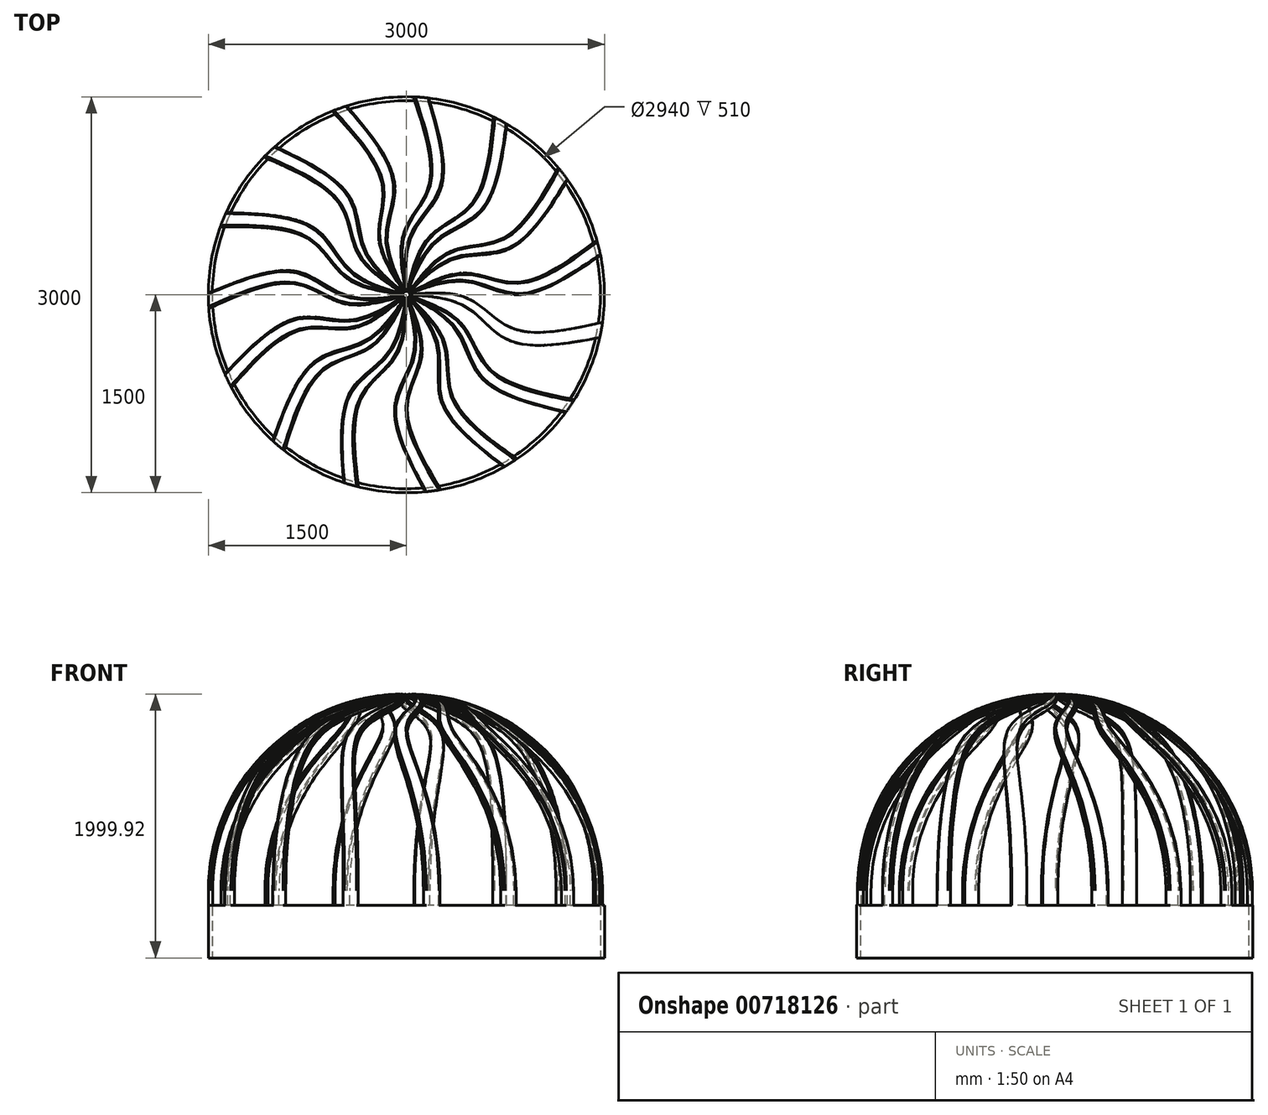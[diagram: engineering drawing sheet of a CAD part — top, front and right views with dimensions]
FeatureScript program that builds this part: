
annotation { "Feature Type Name" : "Feature", "Feature Type Description" : "" }
export const myFeature = defineFeature(function(context is Context, id is Id, definition is map)
    precondition{}
    {
        {
            var Q0;
            Q0=qCreatedBy(makeId("Top.planeOp"),FACE);
            var sketch = newSketch(context, id + "F0", { "sketchPlane" : qUnion([Q0])});
            skCircle(sketch, "E0", {"center": v(0, 0) * mm, "radius": 1500 * mm});
            skSolve(sketch);
        }
        {
            var Q0;
            Q0=makeQuery(id+"F0.imprint","IMPRINT",FACE,{"disambiguationData":[TD([[makeQuery(id+"F0.imprint","IMPRINT",EDGE,{"derivedFrom":sQuery(id+"F0.wireOp",EDGE,"E0")}),1.0]])]});
            extrude(context, id + "F1", {"entities" : qUnion([Q0]), "depth" : 2000 * mm, "offsetDistance" : 25 * mm});
        }
        {
            var Q0;
            Q0=makeQuery(id+"F1.opExtrude","CAP_FACE",FACE,{"disambiguationData":[OSD([sQuery(id+"F0.wireOp",EDGE,"E0")])],"isStart":false});
            fillet(context, id + "F2", {"entities" : qUnion([Q0]), "radius" : 1490 * mm, "tangentPropagation" : true, "allowEdgeOverflow" : false});
        }
        {
            var Q0;
            Q0=makeQuery(id+"F1.opExtrude","CAP_FACE",FACE,{"disambiguationData":[OSD([sQuery(id+"F0.wireOp",EDGE,"E0")])],"isStart":true});
            shell(context, id + "F3", {"entities" : qUnion([Q0]), "thickness" : 30 * mm});
        }
        {
            var Q0;
            Q0=makeQuery(id+"F1.opExtrude","CAP_FACE",FACE,{"disambiguationData":[OSD([sQuery(id+"F0.wireOp",EDGE,"E0")])],"isStart":false});
            var sketch = newSketch(context, id + "F4", { "sketchPlane" : qUnion([Q0])});
            skLineSegment(sketch, "E1", {"start": v(0, 0) * mm, "end": v(0, 0) * mm});
            skFitSpline(sketch, "E2", {"points": [v(0, 0) * mm, v(443.42, 164.47) * mm, v(843.7, 94.34) * mm, v(1455.44, 423.4) * mm], "startDerivative": vector(1720.93, 881.17) * mm, "endDerivative": vector(1641.37, 1335.09) * mm, "construction": true});
            skPoint(sketch, "E3.2.0", {"position": v(338.19, 330.6) * mm});
            skPoint(sketch, "E3.2.1", {"position": v(374.7, 275.35) * mm});
            skPoint(sketch, "E3.2.2", {"position": v(778.83, 346.76) * mm});
            skPoint(sketch, "E3.2.3", {"position": v(732.39, 429.34) * mm});
            skPoint(sketch, "E3.2.4", {"position": v(1157.4, 978.78) * mm});
            skPoint(sketch, "E3.2.5", {"position": v(1235.82, 895.92) * mm});
            skPoint(sketch, "E3.4.0", {"position": v(174.48, 439.57) * mm});
            skPoint(sketch, "E3.4.1", {"position": v(230.3, 403.95) * mm});
            skPoint(sketch, "E3.4.2", {"position": v(570.46, 633.56) * mm});
            skPoint(sketch, "E3.4.3", {"position": v(494.44, 690.11) * mm});
            skPoint(sketch, "E3.4.4", {"position": v(659.23, 1364.92) * mm});
            skPoint(sketch, "E3.4.5", {"position": v(764.57, 1321.12) * mm});
            skPoint(sketch, "E3.6.0", {"position": v(-19.4, 472.54) * mm});
            skPoint(sketch, "E3.6.1", {"position": v(46.1, 462.7) * mm});
            skPoint(sketch, "E3.6.2", {"position": v(263.45, 810.8) * mm});
            skPoint(sketch, "E3.6.3", {"position": v(171, 831.56) * mm});
            skPoint(sketch, "E3.6.4", {"position": v(47.07, 1515.05) * mm});
            skPoint(sketch, "E3.6.5", {"position": v(161.12, 1517.88) * mm});
            skPoint(sketch, "E3.8.0", {"position": v(-209.91, 423.8) * mm});
            skPoint(sketch, "E3.8.1", {"position": v(-146.09, 441.44) * mm});
            skPoint(sketch, "E3.8.2", {"position": v(-89.11, 847.86) * mm});
            skPoint(sketch, "E3.8.3", {"position": v(-182, 829.21) * mm});
            skPoint(sketch, "E3.8.4", {"position": v(-573.22, 1403.21) * mm});
            skPoint(sketch, "E3.8.5", {"position": v(-470.18, 1452.19) * mm});
            skPoint(sketch, "E3.10.0", {"position": v(-364.14, 301.78) * mm});
            skPoint(sketch, "E3.10.1", {"position": v(-313, 343.86) * mm});
            skPoint(sketch, "E3.10.2", {"position": v(-426.27, 738.32) * mm});
            skPoint(sketch, "E3.10.3", {"position": v(-503.55, 683.5) * mm});
            skPoint(sketch, "E3.10.4", {"position": v(-1094.4, 1048.75) * mm});
            skPoint(sketch, "E3.10.5", {"position": v(-1020.19, 1135.4) * mm});
            skPoint(sketch, "E3.12.0", {"position": v(-455.4, 127.58) * mm});
            skPoint(sketch, "E3.12.1", {"position": v(-425.8, 186.82) * mm});
            skPoint(sketch, "E3.12.2", {"position": v(-689.71, 501.1) * mm});
            skPoint(sketch, "E3.12.3", {"position": v(-738.01, 419.6) * mm});
            skPoint(sketch, "E3.12.4", {"position": v(-1426.35, 512.95) * mm});
            skPoint(sketch, "E3.12.5", {"position": v(-1393.8, 622.29) * mm});
            skPoint(sketch, "E3.14.0", {"position": v(-467.92, -68.68) * mm});
            skPoint(sketch, "E3.14.1", {"position": v(-464.98, -2.53) * mm});
            skPoint(sketch, "E3.14.2", {"position": v(-833.9, 177.25) * mm});
            skPoint(sketch, "E3.14.3", {"position": v(-844.87, 83.14) * mm});
            skPoint(sketch, "E3.14.4", {"position": v(-1511.67, -111.55) * mm});
            skPoint(sketch, "E3.14.5", {"position": v(-1526.4, 1.58) * mm});
            skPoint(sketch, "E3.16.0", {"position": v(-399.53, -253.06) * mm});
            skPoint(sketch, "E3.16.1", {"position": v(-423.75, -191.43) * mm});
            skPoint(sketch, "E3.16.2", {"position": v(-833.9, -177.25) * mm});
            skPoint(sketch, "E3.16.3", {"position": v(-805.65, -267.69) * mm});
            skPoint(sketch, "E3.16.4", {"position": v(-1335.6, -716.76) * mm});
            skPoint(sketch, "E3.16.5", {"position": v(-1395.08, -619.4) * mm});
            skPoint(sketch, "E3.18.0", {"position": v(-262.06, -393.7) * mm});
            skPoint(sketch, "E3.18.1", {"position": v(-309.26, -347.24) * mm});
            skPoint(sketch, "E3.18.2", {"position": v(-689.71, -501.1) * mm});
            skPoint(sketch, "E3.18.3", {"position": v(-627.12, -572.23) * mm});
            skPoint(sketch, "E3.18.4", {"position": v(-928.6, -1198.03) * mm});
            skPoint(sketch, "E3.18.5", {"position": v(-1022.54, -1133.28) * mm});
            skPoint(sketch, "E3.20.0", {"position": v(-79.28, -466.24) * mm});
            skPoint(sketch, "E3.20.1", {"position": v(-141.28, -443) * mm});
            skPoint(sketch, "E3.20.2", {"position": v(-426.27, -738.32) * mm});
            skPoint(sketch, "E3.20.3", {"position": v(-340.15, -777.83) * mm});
            skPoint(sketch, "E3.20.4", {"position": v(-361.04, -1472.15) * mm});
            skPoint(sketch, "E3.20.5", {"position": v(-473.19, -1451.2) * mm});
            skPoint(sketch, "E3.22.0", {"position": v(117.22, -458.18) * mm});
            skPoint(sketch, "E3.22.1", {"position": v(51.12, -462.17) * mm});
            skPoint(sketch, "E3.22.2", {"position": v(-89.11, -847.86) * mm});
            skPoint(sketch, "E3.22.3", {"position": v(5.63, -848.94) * mm});
            skPoint(sketch, "E3.22.4", {"position": v(268.95, -1491.73) * mm});
            skPoint(sketch, "E3.22.5", {"position": v(157.98, -1518.2) * mm});
            skPoint(sketch, "E3.24.0", {"position": v(293.44, -370.9) * mm});
            skPoint(sketch, "E3.24.1", {"position": v(234.68, -401.42) * mm});
            skPoint(sketch, "E3.24.2", {"position": v(263.45, -810.8) * mm});
            skPoint(sketch, "E3.24.3", {"position": v(350.44, -773.25) * mm});
            skPoint(sketch, "E3.24.4", {"position": v(852.44, -1253.37) * mm});
            skPoint(sketch, "E3.24.5", {"position": v(761.83, -1322.7) * mm});
            skPoint(sketch, "E3.26.0", {"position": v(418.93, -219.48) * mm});
            skPoint(sketch, "E3.26.1", {"position": v(377.66, -271.27) * mm});
            skPoint(sketch, "E3.26.2", {"position": v(570.46, -633.56) * mm});
            skPoint(sketch, "E3.26.3", {"position": v(634.65, -563.87) * mm});
            skPoint(sketch, "E3.26.4", {"position": v(1288.53, -798.3) * mm});
            skPoint(sketch, "E3.26.5", {"position": v(1233.96, -898.48) * mm});
            skPoint(sketch, "E3.27.3", {"position": v(738.01, -419.6) * mm});
            skPoint(sketch, "E3.28.0", {"position": v(471.98, -30.1) * mm});
            skPoint(sketch, "E3.28.1", {"position": v(455.34, -94.2) * mm});
            skPoint(sketch, "E3.28.2", {"position": v(778.83, -346.76) * mm});
            skPoint(sketch, "E3.28.3", {"position": v(809.13, -256.98) * mm});
            skPoint(sketch, "E3.28.4", {"position": v(1501.83, -205.18) * mm});
            skPoint(sketch, "E3.28.5", {"position": v(1492.72, -318.9) * mm});
            skFitSpline(sketch, "E4", {"points": [v(0, 0) * mm, v(374.7, 275.35) * mm, v(778.83, 346.76) * mm, v(1235.82, 895.92) * mm], "startDerivative": vector(1131.7, 1116.14) * mm, "endDerivative": vector(1100.53, 1804.63) * mm});
            skFitSpline(sketch, "E5", {"points": [v(0, 0) * mm, v(338.19, 330.6) * mm, v(732.39, 429.34) * mm, v(1157.4, 978.78) * mm], "startDerivative": vector(974.1, 1303.77) * mm, "endDerivative": vector(1012.18, 1800.98) * mm});
            skFitSpline(sketch, "E6", {"points": [v(0, 0) * mm, v(230.3, 403.95) * mm, v(570.46, 633.56) * mm, v(764.57, 1321.12) * mm], "startDerivative": vector(579.9, 1479.95) * mm, "endDerivative": vector(271.37, 2096.24) * mm});
            skFitSpline(sketch, "E7", {"points": [v(0, 0) * mm, v(174.48, 439.57) * mm, v(494.44, 690.11) * mm, v(659.23, 1364.92) * mm], "startDerivative": vector(359.6, 1587.25) * mm, "endDerivative": vector(192.15, 2056.97) * mm});
            skFitSpline(sketch, "E8", {"points": [v(0, 0) * mm, v(46.1, 462.7) * mm, v(263.45, 810.8) * mm, v(161.12, 1517.88) * mm], "startDerivative": vector(-72.2, 1587.87) * mm, "endDerivative": vector(-604.7, 2025.39) * mm});
            skFitSpline(sketch, "E9", {"points": [v(0, 0) * mm, v(-19.4, 472.54) * mm, v(171, 831.56) * mm, v(47.07, 1515.05) * mm], "startDerivative": vector(-317.1, 1596.29) * mm, "endDerivative": vector(-661.1, 1957.29) * mm});
            skFitSpline(sketch, "E10", {"points": [v(0, 0) * mm, v(-146.09, 441.44) * mm, v(-89.11, 847.86) * mm, v(-470.18, 1452.19) * mm], "startDerivative": vector(-711.8, 1421.22) * mm, "endDerivative": vector(-1376.22, 1604.33) * mm});
            skFitSpline(sketch, "E11", {"points": [v(0, 0) * mm, v(-209.91, 423.8) * mm, v(-182, 829.21) * mm, v(-573.22, 1403.21) * mm], "startDerivative": vector(-938.95, 1329.3) * mm, "endDerivative": vector(-1400.05, 1519.18) * mm});
            skFitSpline(sketch, "E12", {"points": [v(0, 0) * mm, v(-313, 343.86) * mm, v(-426.27, 738.32) * mm, v(-1020.19, 1135.4) * mm], "startDerivative": vector(-1228.32, 1008.84) * mm, "endDerivative": vector(-1909.78, 905.86) * mm});
            skFitSpline(sketch, "E13", {"points": [v(0, 0) * mm, v(-364.14, 301.78) * mm, v(-503.55, 683.5) * mm, v(-1094.4, 1048.75) * mm], "startDerivative": vector(-1398.45, 832.48) * mm, "endDerivative": vector(-1896.92, 818.38) * mm});
            skFitSpline(sketch, "E14", {"points": [v(0, 0) * mm, v(-425.8, 186.82) * mm, v(-689.71, 501.1) * mm, v(-1393.8, 622.29) * mm], "startDerivative": vector(-1532.46, 422.02) * mm, "endDerivative": vector(-2113.12, 50.77) * mm});
            skFitSpline(sketch, "E15", {"points": [v(0, 0) * mm, v(-455.4, 127.58) * mm, v(-738.01, 419.6) * mm, v(-1426.35, 512.95) * mm], "startDerivative": vector(-1616.15, 191.7) * mm, "endDerivative": vector(-2065.79, -23.92) * mm});
            skFitSpline(sketch, "E16", {"points": [v(0, 0) * mm, v(-464.98, -2.53) * mm, v(-833.9, 177.25) * mm, v(-1526.4, 1.58) * mm], "startDerivative": vector(-1571.62, -237.77) * mm, "endDerivative": vector(-1951.08, -813.1) * mm});
            skFitSpline(sketch, "E17", {"points": [v(0, 0) * mm, v(-467.92, -68.68) * mm, v(-844.87, 83.14) * mm, v(-1511.67, -111.55) * mm], "startDerivative": vector(-1554.4, -482.21) * mm, "endDerivative": vector(-1877.46, -862.08) * mm});
            skFitSpline(sketch, "E18", {"points": [v(0, 0) * mm, v(-423.75, -191.43) * mm, v(-833.9, -177.25) * mm, v(-1395.08, -619.4) * mm], "startDerivative": vector(-1339.04, -856.45) * mm, "endDerivative": vector(-1451.68, -1536.38) * mm});
            skFitSpline(sketch, "E19", {"points": [v(0, 0) * mm, v(-399.53, -253.06) * mm, v(-805.65, -267.69) * mm, v(-1335.6, -716.76) * mm], "startDerivative": vector(-1223.88, -1072.75) * mm, "endDerivative": vector(-1364.5, -1551.18) * mm});
            skFitSpline(sketch, "E20", {"points": [v(0, 0) * mm, v(-309.26, -347.24) * mm, v(-689.71, -501.1) * mm, v(-1022.54, -1133.28) * mm], "startDerivative": vector(-874.92, -1327.04) * mm, "endDerivative": vector(-701.28, -1994) * mm});
            skFitSpline(sketch, "E21", {"points": [v(0, 0) * mm, v(-262.06, -393.7) * mm, v(-627.12, -572.23) * mm, v(-928.6, -1198.03) * mm], "startDerivative": vector(-681.74, -1477.8) * mm, "endDerivative": vector(-615.62, -1972.07) * mm});
            skFitSpline(sketch, "E22", {"points": [v(0, 0) * mm, v(-141.28, -443) * mm, v(-426.27, -738.32) * mm, v(-473.19, -1451.2) * mm], "startDerivative": vector(-259.52, -1568.18) * mm, "endDerivative": vector(170.39, -2106.85) * mm});
            skFitSpline(sketch, "E23", {"points": [v(0, 0) * mm, v(-79.28, -466.24) * mm, v(-340.15, -777.83) * mm, v(-361.04, -1472.15) * mm], "startDerivative": vector(-21.73, -1627.33) * mm, "endDerivative": vector(239.72, -2051.97) * mm});
            skFitSpline(sketch, "E24", {"points": [v(0, 0) * mm, v(51.12, -462.17) * mm, v(-89.11, -847.86) * mm, v(157.98, -1518.2) * mm], "startDerivative": vector(400.75, -1538.16) * mm, "endDerivative": vector(1012.6, -1855.4) * mm});
            skFitSpline(sketch, "E25", {"points": [v(0, 0) * mm, v(117.22, -458.18) * mm, v(5.63, -848.94) * mm, v(268.95, -1491.73) * mm], "startDerivative": vector(642.05, -1495.48) * mm, "endDerivative": vector(1053.6, -1777.07) * mm});
            skFitSpline(sketch, "E26", {"points": [v(0, 0) * mm, v(234.68, -401.42) * mm, v(263.45, -810.8) * mm, v(761.83, -1322.7) * mm], "startDerivative": vector(991.73, -1242.18) * mm, "endDerivative": vector(1679.7, -1283.13) * mm});
            skFitSpline(sketch, "E27", {"points": [v(0, 0) * mm, v(293.44, -370.9) * mm, v(350.44, -773.25) * mm, v(852.44, -1253.37) * mm], "startDerivative": vector(1194.8, -1105.04) * mm, "endDerivative": vector(1685.31, -1194.9) * mm});
            skFitSpline(sketch, "E28", {"points": [v(0, 0) * mm, v(377.66, -271.27) * mm, v(570.46, -633.56) * mm, v(1233.96, -898.48) * mm], "startDerivative": vector(1411.23, -731.41) * mm, "endDerivative": vector(2056.39, -489) * mm});
            skFitSpline(sketch, "E29", {"points": [v(0, 0) * mm, v(418.93, -219.48) * mm, v(634.65, -563.87) * mm, v(1288.53, -798.3) * mm], "startDerivative": vector(1540.97, -523.54) * mm, "endDerivative": vector(2025.62, -406.1) * mm});
            skFitSpline(sketch, "E30", {"points": [v(0, 0) * mm, v(455.34, -94.2) * mm, v(778.83, -346.76) * mm, v(1492.72, -318.9) * mm], "startDerivative": vector(1586.71, -94.18) * mm, "endDerivative": vector(2077.5, 389.68) * mm});
            skFitSpline(sketch, "E31", {"points": [v(-4.96, -0.45) * mm, v(471.98, -30.1) * mm, v(809.13, -256.98) * mm, v(1501.83, -205.18) * mm], "startDerivative": vector(1626.2, 146.66) * mm, "endDerivative": vector(2017.33, 453.02) * mm});
            skFitSpline(sketch, "E32", {"points": [v(0, 0) * mm, v(454.3, 99.15) * mm, v(852.53, 0) * mm, v(1493.38, 315.81) * mm], "startDerivative": vector(1487.84, 559.34) * mm, "endDerivative": vector(1739.4, 1200.99) * mm});
            skFitSpline(sketch, "E33", {"points": [v(0, 0) * mm, v(443.42, 164.47) * mm, v(843.7, 94.34) * mm, v(1455.44, 423.4) * mm], "startDerivative": vector(1420.17, 794.85) * mm, "endDerivative": vector(1657.2, 1233.59) * mm});
            skFitSpline(sketch, "E34.trimOffspring", {"points": [v(0, 0) * mm, v(454.3, 99.15) * mm, v(852.53, 0) * mm, v(1493.38, 315.81) * mm], "startDerivative": vector(1487.84, 559.34) * mm, "endDerivative": vector(1620.1, 1322.46) * mm, "construction": true});
            skArc(sketch, "E35", {"start": v(-19.31, 15.87) * mm, "mid": v(-20.45, 14.38) * mm, "end": v(-21.47, 12.8) * mm});
            skArc(sketch, "E36.trimOffspring", {"start": v(-11.19, 22.36) * mm, "mid": v(-12.84, 21.45) * mm, "end": v(-14.41, 20.43) * mm});
            skArc(sketch, "E37.trimOffspring", {"start": v(-1.13, 24.97) * mm, "mid": v(-3, 24.82) * mm, "end": v(-4.86, 24.52) * mm});
            skArc(sketch, "E38.trimOffspring", {"start": v(9.13, 23.27) * mm, "mid": v(7.35, 23.9) * mm, "end": v(5.54, 24.38) * mm});
            skArc(sketch, "E39.trimOffspring", {"start": v(17.8, 17.55) * mm, "mid": v(16.44, 18.84) * mm, "end": v(14.97, 20.02) * mm});
            skArc(sketch, "E40.trimOffspring", {"start": v(23.4, 8.78) * mm, "mid": v(22.68, 10.52) * mm, "end": v(21.82, 12.2) * mm});
            skArc(sketch, "E41.trimOffspring", {"start": v(24.96, -1.49) * mm, "mid": v(25, 0.37) * mm, "end": v(24.9, 2.23) * mm});
            skArc(sketch, "E42.trimOffspring", {"start": v(22.2, -11.51) * mm, "mid": v(23, -9.81) * mm, "end": v(23.67, -8.05) * mm});
            skArc(sketch, "E43.trimOffspring", {"start": v(15.6, -19.54) * mm, "mid": v(17.02, -18.32) * mm, "end": v(18.34, -16.98) * mm});
            skArc(sketch, "E44.trimOffspring", {"start": v(6.3, -24.2) * mm, "mid": v(8.1, -23.65) * mm, "end": v(9.85, -22.98) * mm});
            skArc(sketch, "E45.trimOffspring", {"start": v(-4.1, -24.66) * mm, "mid": v(-2.22, -24.9) * mm, "end": v(-0.35, -25) * mm});
            skArc(sketch, "E46.trimOffspring", {"start": v(-13.77, -20.87) * mm, "mid": v(-12.16, -21.84) * mm, "end": v(-10.48, -22.7) * mm});
            skArc(sketch, "E47.trimOffspring", {"start": v(-21.07, -13.46) * mm, "mid": v(-20, -15) * mm, "end": v(-18.8, -16.47) * mm});
            skArc(sketch, "E48.trimOffspring", {"start": v(-24.72, -3.73) * mm, "mid": v(-24.37, -5.58) * mm, "end": v(-23.88, -7.4) * mm});
            skArc(sketch, "E49.trimOffspring", {"start": v(-24.1, 6.65) * mm, "mid": v(-24.53, 4.82) * mm, "end": v(-24.82, 2.96) * mm});
            skLineSegment(sketch, "E50", {"start": v(-1511.67, -111.55) * mm, "end": v(-1560.88, -374.04) * mm});
            skLineSegment(sketch, "E51", {"start": v(-1560.88, -374.04) * mm, "end": v(-1395.08, -619.4) * mm});
            skLineSegment(sketch, "E52", {"start": v(-1335.6, -716.76) * mm, "end": v(-1218.07, -1088.2) * mm});
            skLineSegment(sketch, "E53", {"start": v(-1218.07, -1088.2) * mm, "end": v(-1022.54, -1133.28) * mm});
            skLineSegment(sketch, "E54", {"start": v(-1526.4, 1.58) * mm, "end": v(-1643.98, 215.48) * mm});
            skLineSegment(sketch, "E55", {"start": v(-1643.98, 215.48) * mm, "end": v(-1426.35, 512.95) * mm});
            skLineSegment(sketch, "E56", {"start": v(-1393.8, 622.29) * mm, "end": v(-1393.8, 869.3) * mm});
            skLineSegment(sketch, "E57", {"start": v(-1393.8, 869.3) * mm, "end": v(-1094.4, 1048.75) * mm});
            skLineSegment(sketch, "E58", {"start": v(-1020.19, 1135.4) * mm, "end": v(-928.65, 1338.53) * mm});
            skLineSegment(sketch, "E59", {"start": v(-928.65, 1338.53) * mm, "end": v(-573.22, 1403.21) * mm});
            skLineSegment(sketch, "E60", {"start": v(-470.18, 1452.19) * mm, "end": v(-366.73, 1522.16) * mm});
            skLineSegment(sketch, "E61", {"start": v(-366.73, 1522.16) * mm, "end": v(47.07, 1515.05) * mm});
            skLineSegment(sketch, "E62", {"start": v(161.12, 1517.88) * mm, "end": v(408.21, 1517.88) * mm});
            skLineSegment(sketch, "E63", {"start": v(408.21, 1517.88) * mm, "end": v(659.23, 1364.92) * mm});
            skLineSegment(sketch, "E64", {"start": v(764.57, 1321.12) * mm, "end": v(962.79, 1239.37) * mm});
            skLineSegment(sketch, "E65", {"start": v(962.79, 1239.37) * mm, "end": v(1157.4, 978.78) * mm});
            skLineSegment(sketch, "E66", {"start": v(1235.82, 895.92) * mm, "end": v(1487.98, 622.29) * mm});
            skLineSegment(sketch, "E67", {"start": v(1487.98, 622.29) * mm, "end": v(1455.44, 423.4) * mm});
            skLineSegment(sketch, "E68", {"start": v(1493.38, 315.81) * mm, "end": v(1598.16, -111.55) * mm});
            skLineSegment(sketch, "E69", {"start": v(1598.16, -111.55) * mm, "end": v(1501.83, -205.18) * mm});
            skLineSegment(sketch, "E70", {"start": v(1492.72, -318.9) * mm, "end": v(1492.72, -519.85) * mm});
            skLineSegment(sketch, "E71", {"start": v(1492.72, -519.85) * mm, "end": v(1288.53, -798.3) * mm});
            skLineSegment(sketch, "E72", {"start": v(1233.96, -898.48) * mm, "end": v(1157.4, -1081.77) * mm});
            skLineSegment(sketch, "E73", {"start": v(1157.4, -1081.77) * mm, "end": v(852.44, -1253.37) * mm});
            skLineSegment(sketch, "E74", {"start": v(761.83, -1322.7) * mm, "end": v(628.57, -1460.06) * mm});
            skLineSegment(sketch, "E75", {"start": v(628.57, -1460.06) * mm, "end": v(268.95, -1491.73) * mm});
            skLineSegment(sketch, "E76", {"start": v(157.98, -1518.2) * mm, "end": v(-58.22, -1548.2) * mm});
            skLineSegment(sketch, "E77", {"start": v(-58.22, -1548.2) * mm, "end": v(-361.04, -1472.15) * mm});
            skLineSegment(sketch, "E78", {"start": v(-473.19, -1451.2) * mm, "end": v(-895.6, -1390.28) * mm});
            skLineSegment(sketch, "E79", {"start": v(-895.6, -1390.28) * mm, "end": v(-928.6, -1198.03) * mm});
            skSolve(sketch);
        }
        {
            var Q0;
            Q0 = qSketchRegion(id + "F4", true);
            extrude(context, id + "F5", {"entities" : qUnion([Q0]), "operationType" : NewBodyOperationType.REMOVE, "oppositeDirection" : true, "depth" : 1600 * mm, "offsetDistance" : 25 * mm});
        }
        {
            var Q0;
            {var subQ0=sQuery(id+"F0.wireOp",EDGE,"E0");Q0=makeQuery(id+"F5.boolean.opBoolean","SPLIT",FACE,{"disambiguationData":[TD([makeQuery(id+"F5.opExtrude","SWEPT_FACE",FACE,{"disambiguationData":[OSD([sQuery(id+"F4.wireOp",EDGE,"E25")])]})])],"derivedFrom":makeQuery(id+"F2.opFillet","BLEND_FACE",FACE,{"disambiguationData":[OSD([subQ0])]})});}
            var Q1;
            {var subQ0=sQuery(id+"F0.wireOp",EDGE,"E0");Q1=makeQuery(id+"F5.boolean.opBoolean","SPLIT",FACE,{"disambiguationData":[TD([makeQuery(id+"F5.opExtrude","SWEPT_FACE",FACE,{"disambiguationData":[OSD([sQuery(id+"F4.wireOp",EDGE,"E27")])]})])],"derivedFrom":makeQuery(id+"F2.opFillet","BLEND_FACE",FACE,{"disambiguationData":[OSD([subQ0])]})});}
            var Q2;
            {var subQ0=sQuery(id+"F0.wireOp",EDGE,"E0");Q2=makeQuery(id+"F5.boolean.opBoolean","SPLIT",FACE,{"disambiguationData":[TD([makeQuery(id+"F5.opExtrude","SWEPT_FACE",FACE,{"disambiguationData":[OSD([sQuery(id+"F4.wireOp",EDGE,"E29")])]})])],"derivedFrom":makeQuery(id+"F2.opFillet","BLEND_FACE",FACE,{"disambiguationData":[OSD([subQ0])]})});}
            var Q3;
            {var subQ0=sQuery(id+"F0.wireOp",EDGE,"E0");Q3=makeQuery(id+"F5.boolean.opBoolean","SPLIT",FACE,{"disambiguationData":[TD([makeQuery(id+"F5.opExtrude","SWEPT_FACE",FACE,{"disambiguationData":[OSD([sQuery(id+"F4.wireOp",EDGE,"E32")])]})])],"derivedFrom":makeQuery(id+"F2.opFillet","BLEND_FACE",FACE,{"disambiguationData":[OSD([subQ0])]})});}
            var Q4;
            {var subQ0=sQuery(id+"F0.wireOp",EDGE,"E0");Q4=makeQuery(id+"F5.boolean.opBoolean","SPLIT",FACE,{"disambiguationData":[TD([makeQuery(id+"F5.opExtrude","SWEPT_FACE",FACE,{"disambiguationData":[OSD([sQuery(id+"F4.wireOp",EDGE,"E4")])]})])],"derivedFrom":makeQuery(id+"F2.opFillet","BLEND_FACE",FACE,{"disambiguationData":[OSD([subQ0])]})});}
            var Q5;
            {var subQ0=sQuery(id+"F0.wireOp",EDGE,"E0");Q5=makeQuery(id+"F5.boolean.opBoolean","SPLIT",FACE,{"disambiguationData":[TD([makeQuery(id+"F5.opExtrude","SWEPT_FACE",FACE,{"disambiguationData":[OSD([sQuery(id+"F4.wireOp",EDGE,"E5")])]})])],"derivedFrom":makeQuery(id+"F2.opFillet","BLEND_FACE",FACE,{"disambiguationData":[OSD([subQ0])]})});}
            var Q6;
            {var subQ0=sQuery(id+"F0.wireOp",EDGE,"E0");Q6=makeQuery(id+"F5.boolean.opBoolean","SPLIT",FACE,{"disambiguationData":[TD([makeQuery(id+"F5.opExtrude","SWEPT_FACE",FACE,{"disambiguationData":[OSD([sQuery(id+"F4.wireOp",EDGE,"E7")])]})])],"derivedFrom":makeQuery(id+"F2.opFillet","BLEND_FACE",FACE,{"disambiguationData":[OSD([subQ0])]})});}
            var Q7;
            {var subQ0=sQuery(id+"F0.wireOp",EDGE,"E0");Q7=makeQuery(id+"F5.boolean.opBoolean","SPLIT",FACE,{"disambiguationData":[TD([makeQuery(id+"F5.opExtrude","SWEPT_FACE",FACE,{"disambiguationData":[OSD([sQuery(id+"F4.wireOp",EDGE,"E9")])]})])],"derivedFrom":makeQuery(id+"F2.opFillet","BLEND_FACE",FACE,{"disambiguationData":[OSD([subQ0])]})});}
            var Q8;
            {var subQ0=sQuery(id+"F0.wireOp",EDGE,"E0");Q8=makeQuery(id+"F5.boolean.opBoolean","SPLIT",FACE,{"disambiguationData":[TD([makeQuery(id+"F5.opExtrude","SWEPT_FACE",FACE,{"disambiguationData":[OSD([sQuery(id+"F4.wireOp",EDGE,"E11")])]})])],"derivedFrom":makeQuery(id+"F2.opFillet","BLEND_FACE",FACE,{"disambiguationData":[OSD([subQ0])]})});}
            var Q9;
            {var subQ0=sQuery(id+"F0.wireOp",EDGE,"E0");Q9=makeQuery(id+"F5.boolean.opBoolean","SPLIT",FACE,{"disambiguationData":[TD([makeQuery(id+"F5.opExtrude","SWEPT_FACE",FACE,{"disambiguationData":[OSD([sQuery(id+"F4.wireOp",EDGE,"E13")])]})])],"derivedFrom":makeQuery(id+"F2.opFillet","BLEND_FACE",FACE,{"disambiguationData":[OSD([subQ0])]})});}
            var Q10;
            {var subQ0=sQuery(id+"F0.wireOp",EDGE,"E0");Q10=makeQuery(id+"F5.boolean.opBoolean","SPLIT",FACE,{"disambiguationData":[TD([makeQuery(id+"F5.opExtrude","SWEPT_FACE",FACE,{"disambiguationData":[OSD([sQuery(id+"F4.wireOp",EDGE,"E15")])]})])],"derivedFrom":makeQuery(id+"F2.opFillet","BLEND_FACE",FACE,{"disambiguationData":[OSD([subQ0])]})});}
            var Q11;
            {var subQ0=sQuery(id+"F0.wireOp",EDGE,"E0");Q11=makeQuery(id+"F5.boolean.opBoolean","SPLIT",FACE,{"disambiguationData":[TD([makeQuery(id+"F5.opExtrude","SWEPT_FACE",FACE,{"disambiguationData":[OSD([sQuery(id+"F4.wireOp",EDGE,"E17")])]})])],"derivedFrom":makeQuery(id+"F2.opFillet","BLEND_FACE",FACE,{"disambiguationData":[OSD([subQ0])]})});}
            var Q12;
            {var subQ0=sQuery(id+"F0.wireOp",EDGE,"E0");Q12=makeQuery(id+"F5.boolean.opBoolean","SPLIT",FACE,{"disambiguationData":[TD([makeQuery(id+"F5.opExtrude","SWEPT_FACE",FACE,{"disambiguationData":[OSD([sQuery(id+"F4.wireOp",EDGE,"E19")])]})])],"derivedFrom":makeQuery(id+"F2.opFillet","BLEND_FACE",FACE,{"disambiguationData":[OSD([subQ0])]})});}
            var Q13;
            {var subQ0=sQuery(id+"F0.wireOp",EDGE,"E0");Q13=makeQuery(id+"F5.boolean.opBoolean","SPLIT",FACE,{"disambiguationData":[TD([makeQuery(id+"F5.opExtrude","SWEPT_FACE",FACE,{"disambiguationData":[OSD([sQuery(id+"F4.wireOp",EDGE,"E21")])]})])],"derivedFrom":makeQuery(id+"F2.opFillet","BLEND_FACE",FACE,{"disambiguationData":[OSD([subQ0])]})});}
            var Q14;
            {var subQ0=sQuery(id+"F0.wireOp",EDGE,"E0");Q14=makeQuery(id+"F5.boolean.opBoolean","SPLIT",FACE,{"disambiguationData":[TD([makeQuery(id+"F5.opExtrude","SWEPT_FACE",FACE,{"disambiguationData":[OSD([sQuery(id+"F4.wireOp",EDGE,"E23")])]})])],"derivedFrom":makeQuery(id+"F2.opFillet","BLEND_FACE",FACE,{"disambiguationData":[OSD([subQ0])]})});}
            fillet(context, id + "F6", {"entities" : qUnion([Q0, Q1, Q2, Q3, Q4, Q5, Q6, Q7, Q8, Q9, Q10, Q11, Q12, Q13, Q14]), "radius" : 10 * mm, "tangentPropagation" : true, "allowEdgeOverflow" : false});
        }
    });
